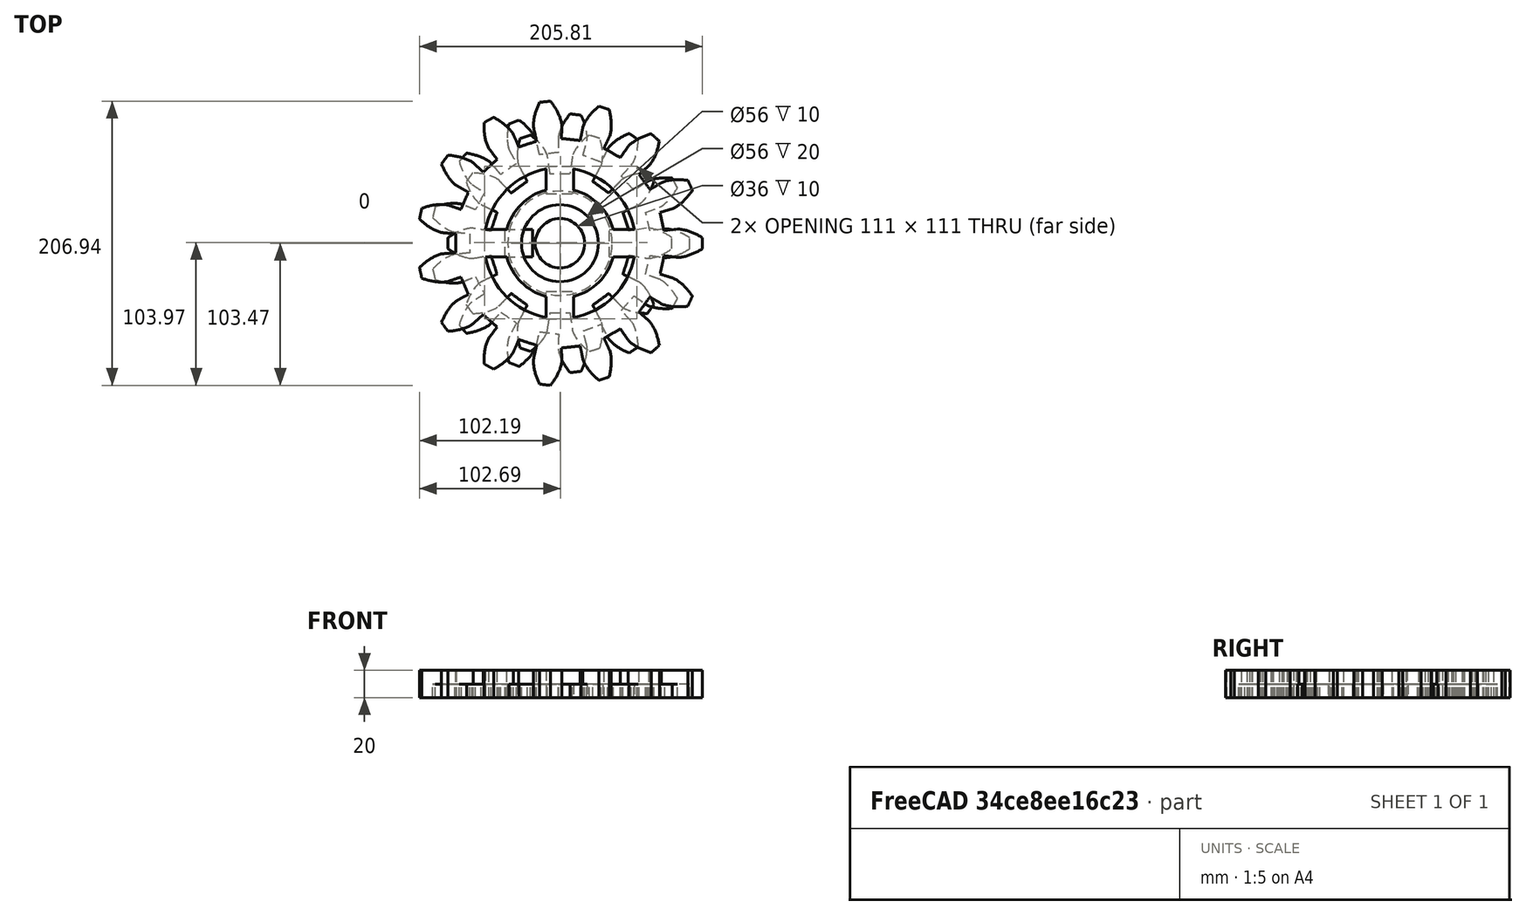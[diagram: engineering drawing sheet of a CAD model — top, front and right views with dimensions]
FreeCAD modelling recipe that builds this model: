
FCSTD DOCUMENT  (FreeCAD 0.20R29177 +426 (Git))
Label: gears
License: All rights reserved
LicenseURL: http://en.wikipedia.org/wiki/All_rights_reserved
objects: Part::Box×16, Part::FeaturePython×8, Part::Cylinder×4, Part::Cut×3, Part::MultiFuse×3
note: 34 computed .brp shape members not serialized (recipe doc carries the construction recipe); baked Part::Feature solids carry a one-line shape summary decoded from their .brp

FEATURE [Part::FeaturePython] InvoluteGear  # WARN: FeaturePython — macro-defined, semantics opaque (R4)
  AttacherType = Attacher::AttachEngine3D
  angular_backlash = 0
  backlash = 0
  beta = 0
  clearance = 0.25
  da = 189
  df = 132.3
  double_helix = false
  dw = 163.8
  head = 0
  head_fillet = 0
  height = 10
  module = 12.6
  numpoints = 6
  pressure_angle = 20
  properties_from_tool = false
  reversed_backlash = false
  root_fillet = 0
  shift = 0
  simple = false
  teeth = 13
  transverse_pitch = 39.5841
  traverse_module = 12.6
  undercut = false
  version = 0.0.4
  expr: angular_backlash = backlash / dw * 360° / pi
FEATURE [Part::Cylinder] Cylinder
  Angle = 360
  AttacherType = Attacher::AttachEngine3D
  FirstAngle = 0
  Height = 10
  Radius = 55
  SecondAngle = 0
FEATURE [Part::FeaturePython] Tube  # WARN: FeaturePython — macro-defined, semantics opaque (R4)
  AttacherType = Attacher::AttachEngine3D
  Height = 10
  InnerRadius = 28
  OuterRadius = 40
FEATURE [Part::Box] Box  label="Cube"
  AttacherType = Attacher::AttachEngine3D
  Height = 10
  Length = 20
  Placement = pos=(-10,-55,0) rot=(0,0,1;0rad)
  Width = 20
FEATURE [Part::Box] Box001  label="Cube001"
  AttacherType = Attacher::AttachEngine3D
  Height = 10
  Length = 20
  Placement = pos=(-10,36,0) rot=(0,0,1;0rad)
  Width = 20
FEATURE [Part::Box] Box002  label="Cube002"
  AttacherType = Attacher::AttachEngine3D
  Height = 10
  Length = 20
  Placement = pos=(-55,-10,0) rot=(0,0,1;0rad)
  Width = 20
FEATURE [Part::Box] Box003  label="Cube003"
  AttacherType = Attacher::AttachEngine3D
  Height = 10
  Length = 20
  Placement = pos=(36,-10,0) rot=(0,0,1;0rad)
  Width = 20
FEATURE [Part::Box] Box004  label="Cube004"
  AttacherType = Attacher::AttachEngine3D
  Height = 10
  Length = 20
  Placement = pos=(-10,-55,0) rot=(0,0,1;0rad)
  Width = 20
FEATURE [Part::Box] Box005  label="Cube005"
  AttacherType = Attacher::AttachEngine3D
  Height = 10
  Length = 20
  Placement = pos=(-10,36,0) rot=(0,0,1;0rad)
  Width = 20
FEATURE [Part::Box] Box006  label="Cube006"
  AttacherType = Attacher::AttachEngine3D
  Height = 10
  Length = 20
  Placement = pos=(-55,-10,0) rot=(0,0,1;0rad)
  Width = 20
FEATURE [Part::Box] Box007  label="Cube007"
  AttacherType = Attacher::AttachEngine3D
  Height = 10
  Length = 20
  Placement = pos=(36,-10,0) rot=(0,0,1;0rad)
  Width = 20
FEATURE [Part::Cylinder] Cylinder001
  Angle = 360
  AttacherType = Attacher::AttachEngine3D
  FirstAngle = 0
  Height = 10
  Radius = 55
  SecondAngle = 0
FEATURE [Part::FeaturePython] InvoluteGear001  # WARN: FeaturePython — macro-defined, semantics opaque (R4)
  AttacherType = Attacher::AttachEngine3D
  angular_backlash = 0
  backlash = 0
  beta = 0
  clearance = 0.25
  da = 189
  df = 132.3
  double_helix = false
  dw = 163.8
  head = 0
  head_fillet = 0
  height = 10
  module = 12.6
  numpoints = 6
  pressure_angle = 20
  properties_from_tool = false
  reversed_backlash = false
  root_fillet = 0
  shift = 0
  simple = false
  teeth = 13
  transverse_pitch = 39.5841
  traverse_module = 12.6
  undercut = false
  version = 0.0.4
  expr: angular_backlash = backlash / dw * 360° / pi
FEATURE [Part::Cut] Cut001
  Base = -> InvoluteGear001
  Tool = -> Cylinder001
FEATURE [Part::FeaturePython] Tube001  # WARN: FeaturePython — macro-defined, semantics opaque (R4)
  AttacherType = Attacher::AttachEngine3D
  Height = 10
  InnerRadius = 23
  OuterRadius = 38
FEATURE [Part::MultiFuse] Fusion001  label="MotorGear"
  Shapes = -> [Tube001,Cut001,Box004,Box005,Box006,Box007]
FEATURE [Part::Cut] Cut
  Base = -> InvoluteGear
  Tool = -> Cylinder
FEATURE [Part::MultiFuse] Fusion  label="WheelGear"
  Shapes = -> [Tube,Box,Box001,Box002,Box003,Cut]
FEATURE [Part::Box] Box008  label="Cube008"
  AttacherType = Attacher::AttachEngine3D
  Height = 10
  Length = 20
  Placement = pos=(-10,-55,0) rot=(0,0,1;0rad)
  Width = 20
FEATURE [Part::Box] Box009  label="Cube009"
  AttacherType = Attacher::AttachEngine3D
  Height = 10
  Length = 20
  Placement = pos=(-10,36,0) rot=(0,0,1;0rad)
  Width = 20
FEATURE [Part::Box] Box010  label="Cube010"
  AttacherType = Attacher::AttachEngine3D
  Height = 10
  Length = 20
  Placement = pos=(-40,-10,0) rot=(0,0,1;0rad)
  Width = 20
FEATURE [Part::Box] Box011  label="Cube011"
  AttacherType = Attacher::AttachEngine3D
  Height = 10
  Length = 20
  Placement = pos=(36,-10,0) rot=(0,0,1;0rad)
  Width = 20
FEATURE [Part::Cylinder] Cylinder002
  Angle = 360
  AttacherType = Attacher::AttachEngine3D
  FirstAngle = 0
  Height = 10
  Radius = 38
  SecondAngle = 0
FEATURE [Part::FeaturePython] InvoluteGear002  # WARN: FeaturePython — macro-defined, semantics opaque (R4)
  AttacherType = Attacher::AttachEngine3D
  angular_backlash = 0
  backlash = 0
  beta = 0
  clearance = 0.25
  da = 163.2
  df = 102
  double_helix = false
  dw = 136
  head = 0
  head_fillet = 0
  height = 10
  module = 13.6
  numpoints = 6
  pressure_angle = 20
  properties_from_tool = false
  reversed_backlash = false
  root_fillet = 0
  shift = 0
  simple = false
  teeth = 10
  transverse_pitch = 42.7257
  traverse_module = 13.6
  undercut = false
  version = 0.0.4
  expr: angular_backlash = backlash / dw * 360° / pi
FEATURE [Part::FeaturePython] Tube002  # WARN: FeaturePython — macro-defined, semantics opaque (R4)
  AttacherType = Attacher::AttachEngine3D
  Height = 10
  InnerRadius = 18
  OuterRadius = 28
FEATURE [Part::Box] Box012  label="Cube012"
  AttacherType = Attacher::AttachEngine3D
  Height = 20
  Length = 20
  Placement = pos=(-10,-55,0) rot=(0,0,1;0rad)
  Width = 20
FEATURE [Part::Box] Box013  label="Cube013"
  AttacherType = Attacher::AttachEngine3D
  Height = 20
  Length = 20
  Placement = pos=(-10,36,0) rot=(0,0,1;0rad)
  Width = 20
FEATURE [Part::Box] Box014  label="Cube014"
  AttacherType = Attacher::AttachEngine3D
  Height = 20
  Length = 20
  Placement = pos=(-55,-10,0) rot=(0,0,1;0rad)
  Width = 20
FEATURE [Part::Box] Box015  label="Cube015"
  AttacherType = Attacher::AttachEngine3D
  Height = 20
  Length = 20
  Placement = pos=(36,-10,0) rot=(0,0,1;0rad)
  Width = 20
FEATURE [Part::Cylinder] Cylinder003
  Angle = 360
  AttacherType = Attacher::AttachEngine3D
  FirstAngle = 0
  Height = 20
  Radius = 55
  SecondAngle = 0
FEATURE [Part::FeaturePython] InvoluteGear003  # WARN: FeaturePython — macro-defined, semantics opaque (R4)
  AttacherType = Attacher::AttachEngine3D
  angular_backlash = 0
  backlash = 0
  beta = 0
  clearance = 0.25
  da = 207.4
  df = 152.5
  double_helix = false
  dw = 183
  head = 0
  head_fillet = 0
  height = 20
  module = 12.2
  numpoints = 6
  pressure_angle = 20
  properties_from_tool = false
  reversed_backlash = false
  root_fillet = 0
  shift = 0
  simple = false
  teeth = 15
  transverse_pitch = 38.3274
  traverse_module = 12.2
  undercut = false
  version = 0.0.4
  expr: angular_backlash = backlash / dw * 360° / pi
FEATURE [Part::Cut] Cut003
  Base = -> InvoluteGear003
  Tool = -> Cylinder003
FEATURE [Part::FeaturePython] Tube003  # WARN: FeaturePython — macro-defined, semantics opaque (R4)
  AttacherType = Attacher::AttachEngine3D
  Height = 20
  InnerRadius = 28
  OuterRadius = 40
FEATURE [Part::MultiFuse] Fusion003  label="WheelGearMore"
  Shapes = -> [Tube003,Box012,Box013,Box014,Box015,Cut003]
